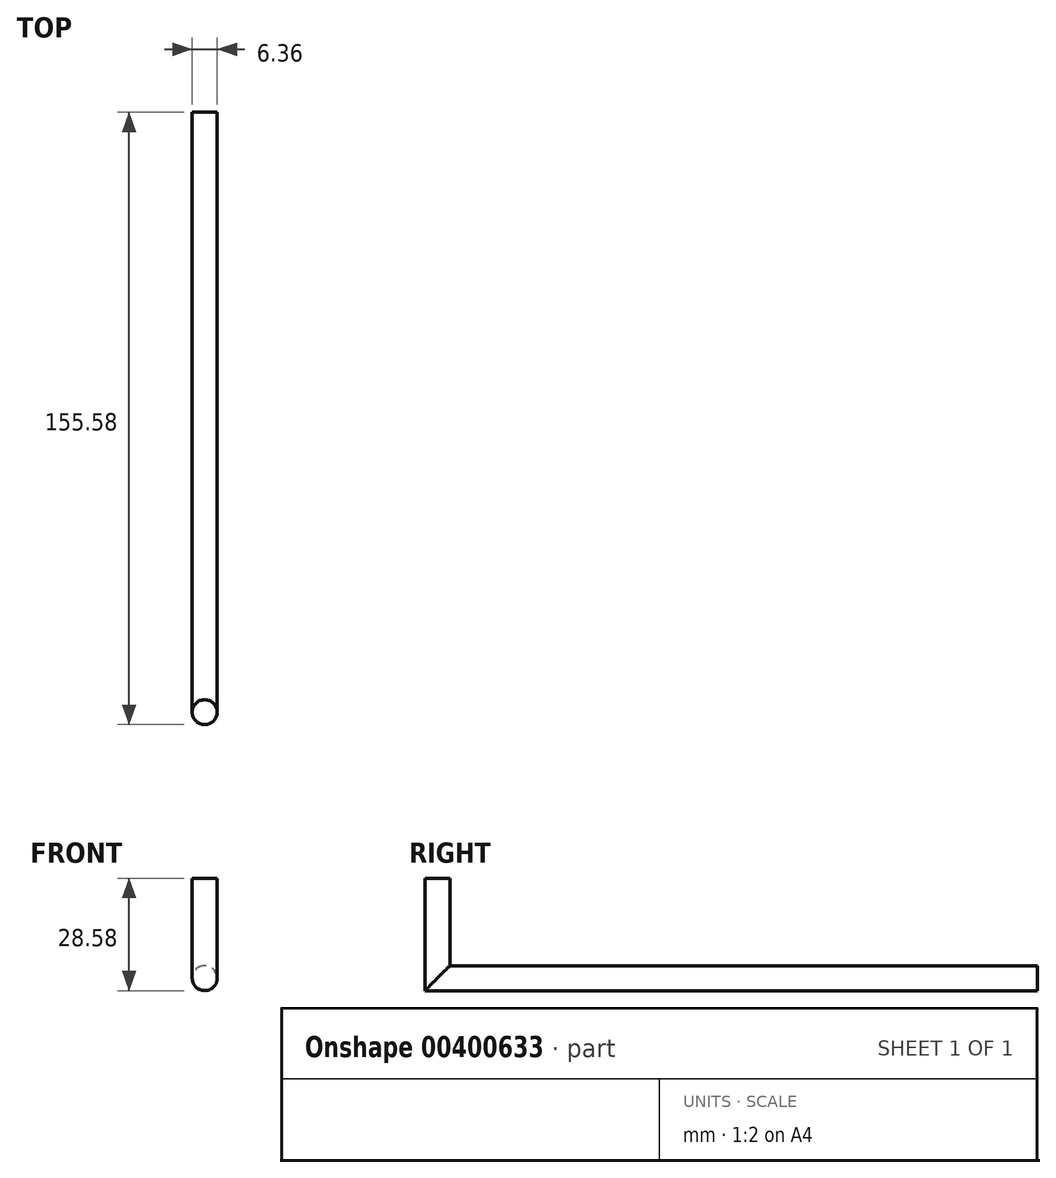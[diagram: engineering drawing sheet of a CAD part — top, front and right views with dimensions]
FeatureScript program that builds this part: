
annotation { "Feature Type Name" : "Feature", "Feature Type Description" : "" }
export const myFeature = defineFeature(function(context is Context, id is Id, definition is map)
    precondition{}
    {
        {
            var Q0;
            Q0=qCreatedBy(makeId("Front.planeOp"),FACE);
            var sketch = newSketch(context, id + "F0", { "sketchPlane" : qUnion([Q0])});
            skCircle(sketch, "E0", {"center": v(0, 0) * mm, "radius": 3.18 * mm});
            skSolve(sketch);
        }
        {
            var Q0;
            Q0=qCreatedBy(makeId("Right.planeOp"),FACE);
            var sketch = newSketch(context, id + "F1", { "sketchPlane" : qUnion([Q0])});
            skLineSegment(sketch, "E1", {"start": v(0, 0) * mm, "end": v(-152.4, 0) * mm});
            skLineSegment(sketch, "E2", {"start": v(-152.4, 0) * mm, "end": v(-152.4, 25.4) * mm});
            skSolve(sketch);
        }
        {
            var Q0;
            Q0=makeQuery(id+"F0.imprint","IMPRINT",FACE,{"disambiguationData":[TD([[makeQuery(id+"F0.imprint","IMPRINT",EDGE,{"derivedFrom":sQuery(id+"F0.wireOp",EDGE,"E0")}),1.0]])]});
            var Q1;
            Q1=sQuery(id+"F1.wireOp",EDGE,"E1");
            var Q2;
            Q2=sQuery(id+"F1.wireOp",EDGE,"E2");
            sweep(context, id + "F2", {"profiles" : qUnion([Q0]), "path" : qUnion([Q1, Q2])});
        }
    });
